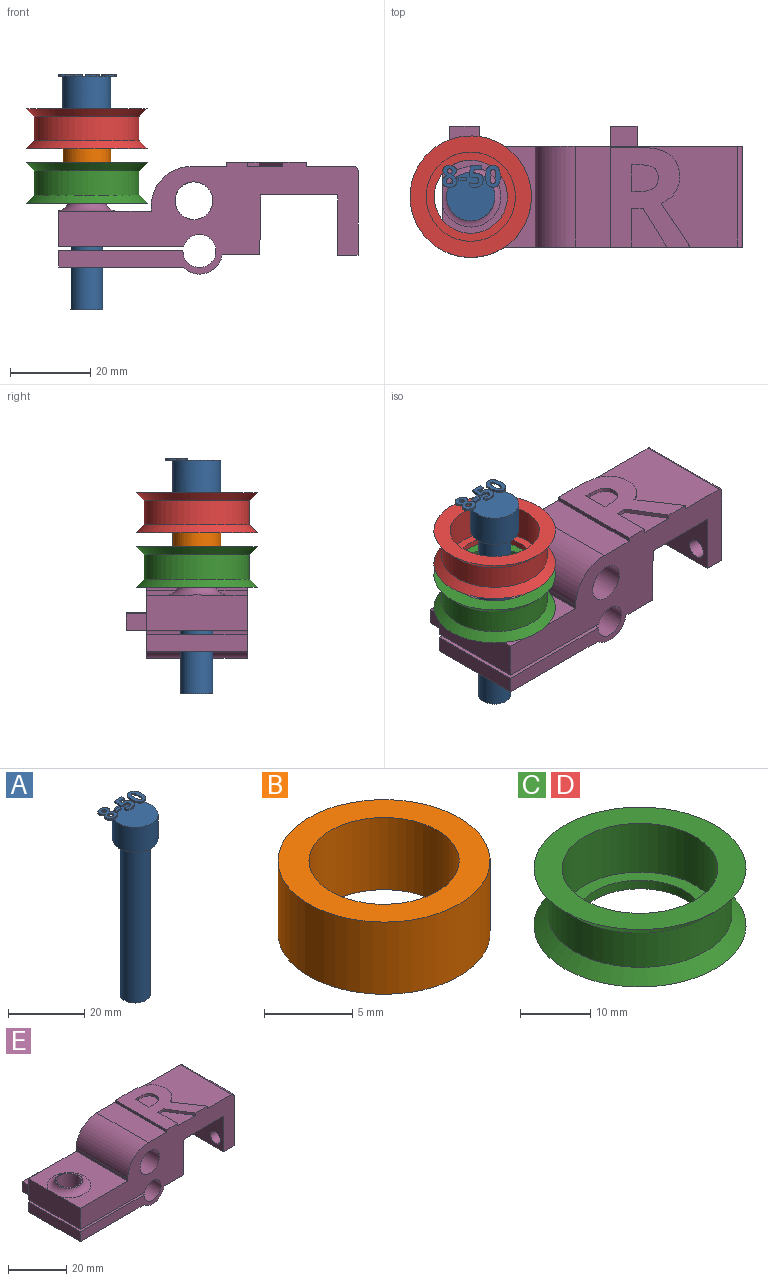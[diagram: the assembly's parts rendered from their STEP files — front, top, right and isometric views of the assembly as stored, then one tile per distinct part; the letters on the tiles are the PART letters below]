
ASSEMBLY  parts=5 mates=4
PART A: 86 faces, bbox 14.5x13.7x58.5 mm
  f0: plane 12x12mm, normal (0,0,1), area 99.4mm2, adj f5,f22,f23,f24,f25,f26,f40,f41
  f1: plane 1x0.26mm, normal (0,0,1), area 0.1mm2, adj f5,f46,f47,f48,f49
  f2: plane 0.85x0.68mm, normal (0,0,1), area 0.2mm2, adj f5,f29,f30,f31
  f3: cylinder r=4mm len=50mm, axis (0,0,-1), area 1256.6mm2, adj f4,f6
  f4: plane 8x8mm, normal (0,0,-1), area 50.3mm2, adj f3
  f5: cylinder r=6mm len=12mm, axis (0,0,-1), area 301.6mm2, adj f0,f1,f2,f6,f39,f45,f67,f85
  f6: plane 12x12mm, normal (0,0,-1), area 62.8mm2, adj f3,f5
  f7: extruded ~0.5x0.46mm, area 0.2mm2, adj f8,f37,f38,f39
  f8: extruded ~0.5x0.46mm, area 0.2mm2, adj f7,f9,f38,f39
  f9: extruded ~0.5x0.39mm, area 0.2mm2, adj f8,f10,f38,f39
  f10: extruded ~0.5x0.4mm, area 0.2mm2, adj f9,f11,f38,f39
  f11: extruded ~0.5x0.49mm, area 0.3mm2, adj f10,f12,f38,f39
  f12: extruded ~0.5x0.5mm, area 0.3mm2, adj f11,f13,f38,f39
  f13: extruded ~0.5x0.39mm, area 0.2mm2, adj f12,f37,f38,f39
  f14: extruded ~1.22x0.5mm, area 0.6mm2, adj f15,f35,f38,f39
  f15: extruded ~1.22x0.5mm, area 0.6mm2, adj f14,f16,f38,f39
  f16: extruded ~0.91x0.5mm, area 0.5mm2, adj f15,f17,f38,f39
  f17: extruded ~0.71x0.5mm, area 0.4mm2, adj f16,f18,f38,f39
  f18: extruded ~0.65x0.61mm, area 0.4mm2, adj f17,f19,f38,f39
  f19: extruded ~0.77x0.62mm, area 0.5mm2, adj f18,f20,f38,f39
  f20: extruded ~0.8x0.5mm, area 0.4mm2, adj f19,f21,f38,f39
  f21: extruded ~1.04x0.5mm, area 0.6mm2, adj f20,f22,f38,f39
  f22: extruded ~1.36x0.5mm, area 0.7mm2, adj f0,f21,f23,f38,f39
  f23: extruded ~1.33x0.5mm, area 0.7mm2, adj f0,f22,f24,f38
  f24: extruded ~1.04x0.51mm, area 0.6mm2, adj f0,f23,f25,f38
  f25: extruded ~0.75x0.5mm, area 0.4mm2, adj f0,f24,f26,f38
  f26: extruded ~0.85x0.66mm, area 0.5mm2, adj f0,f25,f27,f38,f39
  f27: extruded ~0.72x0.56mm, area 0.5mm2, adj f26,f28,f38,f39
  f28: extruded ~0.72x0.5mm, area 0.4mm2, adj f27,f35,f38,f39
  f29: extruded ~0.5x0.45mm, area 0.3mm2, adj f2,f30,f36,f38,f39
  f30: extruded ~0.5x0.47mm, area 0.3mm2, adj f2,f29,f31,f38
  f31: extruded ~0.62x0.5mm, area 0.3mm2, adj f2,f30,f32,f38,f39
  f32: extruded ~0.59x0.5mm, area 0.3mm2, adj f31,f33,f38,f39
  f33: extruded ~0.5x0.48mm, area 0.3mm2, adj f32,f34,f38,f39
  f34: extruded ~0.89x0.77mm, area 0.6mm2, adj f33,f36,f38,f39
  f35: extruded ~0.93x0.5mm, area 0.5mm2, adj f14,f28,f38,f39
  f36: extruded ~0.66x0.5mm, area 0.4mm2, adj f29,f34,f38,f39
  f37: extruded ~0.5x0.39mm, area 0.2mm2, adj f7,f13,f38,f39
  f38: plane 5.4x3.69mm, normal (0,0,1), area 12.7mm2, adj f7,f8,f9,f10,f11,f12,f13,f14
  f39: plane 5.4x3.53mm, normal (0,0,-1), area 10.2mm2, adj f5,f7,f8,f9,f10,f11,f12,f13
  f40: plane 0.9x0.5mm, normal (-1,0,0), area 0.4mm2, adj f0,f41,f43,f44
  f41: plane 1.93x0.5mm, normal (0,-1,0), area 1mm2, adj f0,f40,f42,f44
  f42: plane 0.9x0.5mm, normal (1,0,0), area 0.4mm2, adj f0,f41,f43,f44
  f43: plane 1.93x0.5mm, normal (0,1,0), area 1mm2, adj f0,f40,f42,f44
  f44: plane 1.93x0.9mm, normal (0,0,1), area 1.7mm2, adj f40,f41,f42,f43
  f45: plane 0.76x0.31mm, normal (0,0,-1), area 0mm2, adj f5,f46
  f46: extruded ~1.21x0.5mm, area 0.7mm2, adj f0,f1,f45,f47,f65,f66
  f47: extruded ~0.54x0.5mm, area 0.3mm2, adj f1,f46,f48,f66
  f48: plane 0.5x0.13mm, normal (-0.2,0.98,0), area 0.1mm2, adj f1,f47,f49,f66
  f49: plane 1.03x0.5mm, normal (1,-0.09,0), area 0.5mm2, adj f1,f48,f50,f66,f67
  f50: plane 1.88x0.5mm, normal (0,-1,0), area 0.9mm2, adj f49,f51,f66,f67
  f51: plane 0.94x0.5mm, normal (1,0,0), area 0.5mm2, adj f50,f52,f66,f67
  f52: plane 2.85x0.5mm, normal (0,1,0), area 1.4mm2, adj f51,f53,f66,f67
  f53: plane 2.68x0.5mm, normal (-1,0.07,0), area 1.3mm2, adj f0,f52,f54,f66,f67
  f54: plane 0.5x0.44mm, normal (-0.47,-0.88,0), area 0.3mm2, adj f0,f53,f55,f66
  f55: extruded ~0.5x0.37mm, area 0.2mm2, adj f0,f54,f56,f66
  f56: extruded ~0.5x0.42mm, area 0.2mm2, adj f0,f55,f57,f66
  f57: extruded ~1.05x0.8mm, area 0.8mm2, adj f0,f56,f58,f66
  f58: extruded ~1.02x0.83mm, area 0.8mm2, adj f0,f57,f59,f66
  f59: extruded ~0.72x0.5mm, area 0.4mm2, adj f0,f58,f60,f66
  f60: extruded ~0.66x0.5mm, area 0.4mm2, adj f0,f59,f61,f66
  f61: plane 0.96x0.5mm, normal (-1,0,0), area 0.5mm2, adj f0,f60,f62,f66
  f62: extruded ~1.42x0.5mm, area 0.7mm2, adj f0,f61,f63,f66
  f63: extruded ~1.55x0.5mm, area 0.8mm2, adj f0,f62,f64,f66
  f64: extruded ~1.36x0.54mm, area 0.8mm2, adj f0,f63,f65,f66
  f65: extruded ~1.17x0.5mm, area 0.6mm2, adj f0,f46,f64,f66
  f66: plane 5.33x3.51mm, normal (0,0,1), area 10.9mm2, adj f46,f47,f48,f49,f50,f51,f52,f53
  f67: plane 2.97x1.71mm, normal (0,0,-1), area 3.5mm2, adj f5,f49,f50,f51,f52,f53
  f68: extruded ~1.39x0.5mm, area 0.7mm2, adj f69,f83,f84,f85
  f69: extruded ~1.39x0.5mm, area 0.7mm2, adj f68,f70,f84,f85
  f70: extruded ~0.56x0.5mm, area 0.4mm2, adj f69,f71,f84,f85
  f71: extruded ~0.56x0.5mm, area 0.4mm2, adj f70,f72,f84,f85
  f72: extruded ~1.39x0.5mm, area 0.7mm2, adj f71,f73,f84,f85
  f73: extruded ~1.38x0.5mm, area 0.7mm2, adj f72,f74,f84,f85
  f74: extruded ~0.56x0.5mm, area 0.4mm2, adj f73,f83,f84,f85
  f75: extruded ~2.04x0.5mm, area 1.1mm2, adj f76,f82,f84,f85
  f76: extruded ~2.02x0.5mm, area 1.1mm2, adj f75,f77,f84,f85
  f77: extruded ~1.38x0.69mm, area 0.8mm2, adj f76,f78,f84,f85
  f78: extruded ~1.38x0.66mm, area 0.8mm2, adj f77,f79,f84,f85
  f79: extruded ~2.05x0.5mm, area 1.1mm2, adj f78,f80,f84,f85
  f80: extruded ~2.02x0.5mm, area 1mm2, adj f0,f79,f81,f84,f85
  f81: extruded ~1.37x0.68mm, area 0.8mm2, adj f0,f80,f82,f84
  f82: extruded ~1.39x0.66mm, area 0.8mm2, adj f0,f75,f81,f84,f85
  f83: extruded ~0.56x0.5mm, area 0.4mm2, adj f68,f74,f84,f85
  f84: plane 5.41x3.68mm, normal (0,0,1), area 12.1mm2, adj f68,f69,f70,f71,f72,f73,f74,f75
  f85: plane 5.41x3.68mm, normal (0,0,-1), area 10.3mm2, adj f5,f68,f69,f70,f71,f72,f73,f74
PART B: 4 faces, bbox 12x12x5 mm
  f0: cylinder r=4.25mm len=8.5mm, axis (0,0,-1), area 133.5mm2, adj f2,f3
  f1: cylinder r=6mm len=12mm, axis (0,0,-1), area 188.5mm2, adj f2,f3
  f2: plane 12x12mm, normal (0,0,1), area 56.4mm2, adj f0,f1
  f3: plane 12x12mm, normal (0,0,-1), area 56.4mm2, adj f0,f1
PART C: 8 faces, bbox 30.2x30.2x10 mm
  f0: plane 30.2x30.2mm, normal (0,0,1), area 329.2mm2, adj f1,f7
  f1: cylinder r=11.1mm len=22.2mm, axis (0,0,-1), area 592.8mm2, adj f0,f2
  f2: plane 22.2x22.2mm, normal (0,0,1), area 126.9mm2, adj f1,f3
  f3: cylinder r=9.1mm len=18.2mm, axis (0,0,-1), area 85.8mm2, adj f2,f4
  f4: plane 30.2x30.2mm, normal (0,0,-1), area 456.2mm2, adj f3,f5
  f5: cone r=13.1mm half-angle=45deg, axis (0,0,-1), area 250.6mm2, adj f4,f6
  f6: cylinder r=13.1mm len=26.2mm, axis (0,0,-1), area 493.9mm2, adj f5,f7
  f7: cone r=15.1mm half-angle=45deg, axis (0,0,1), area 250.6mm2, adj f0,f6
PART D: same geometry as C
PART E: 56 faces, bbox 77.9x30x27.7 mm
  f0: plane 40.42x25mm, normal (0,0,1), area 617.1mm2, adj f14,f15,f25,f27,f40,f41,f42,f43
  f1: plane 9.51x8.71mm, normal (0,0,1), area 54.7mm2, adj f14,f37,f38,f39
  f2: plane 25x4.12mm, normal (-1,0,0), area 103mm2, adj f5,f14,f15,f19
  f3: cylinder r=4.17mm len=8.35mm, axis (0,0,1), area 108.1mm2, adj f5,f19
  f4: plane 25x9.34mm, normal (0,0,-1), area 233.4mm2, adj f13,f14,f15,f17
  f5: plane 30.88x25mm, normal (0,0,-1), area 717.2mm2, adj f2,f3,f14,f15,f17
  f6: plane 25x8.82mm, normal (-1,0,0), area 219.6mm2, adj f7,f14,f15,f20,f24
  f7: plane 25x23mm, normal (0,0,1), area 400mm2, adj f6,f8,f14,f15,f24
  f8: plane 25x1.1mm, normal (-1,0,0), area 27.5mm2, adj f7,f14,f15,f25
  f9: plane 25x21.09mm, normal (1,0,0), area 493.5mm2, adj f10,f14,f15,f22,f23,f27
  f10: plane 25x5mm, normal (0,0,-1), area 125mm2, adj f9,f11,f14,f15
  f11: plane 25x15mm, normal (-1,0,0), area 341.3mm2, adj f10,f12,f14,f15,f22,f23
  f12: plane 25x19.2mm, normal (0,0,-1), area 480mm2, adj f11,f13,f14,f15
  f13: plane 25x14.91mm, normal (1,0,-0.01), area 372.8mm2, adj f4,f12,f14,f15
  f14: plane 74.42x27.75mm, normal (0,-1,0), area 1061.7mm2, adj f0,f1,f2,f4,f5,f6,f7,f8
  f15: plane 74.42x26.75mm, normal (0,1,0), area 990.6mm2, adj f0,f2,f4,f5,f6,f7,f8,f9
  f16: cylinder r=4.17mm len=10.78mm, axis (0,0,1), area 282.8mm2, adj f20,f21
  f17: cylinder r=5.75mm len=25mm, axis (0,-1,0), area 315.9mm2, adj f4,f5,f14,f15
  f18: cylinder r=4.1mm len=25mm, axis (0,-1,0), area 618.7mm2, adj f14,f15,f19,f20
  f19: plane 30.91x25mm, normal (0,0,1), area 718.1mm2, adj f2,f3,f14,f15,f18
  f20: plane 31.07x30mm, normal (0,0,-1), area 758.4mm2, adj f6,f14,f15,f16,f18,f29,f30,f31
  f21: plane 9.35x9.35mm, normal (0,0,1), area 13.9mm2, adj f16,f24
  f22: cylinder r=2.43mm len=5mm, axis (1,0,0), area 76.2mm2, adj f9,f11
  f23: cylinder r=2.2mm len=5mm, axis (1,0,0), area 69.1mm2, adj f9,f11
  f24: torus R=7.5mm, axis (0,0,-1), area 134.6mm2, adj f6,f7,f21
  f25: cylinder r=10mm len=25mm, axis (0,-1,0), area 392.7mm2, adj f0,f8,f14,f15
  f26: cylinder r=4.68mm len=25mm, axis (0,-1,0), area 735.2mm2, adj f14,f15
  f27: cylinder r=1mm len=25mm, axis (0,-1,0), area 39.3mm2, adj f0,f9,f14,f15
  f28: plane 7.3x5mm, normal (0,0,1), area 36.5mm2, adj f15,f29,f30,f31
  f29: plane 5x4.12mm, normal (-1,0,0), area 20.6mm2, adj f15,f20,f28,f31
  f30: plane 5x4.12mm, normal (1,0,0), area 20.6mm2, adj f15,f20,f28,f31
  f31: plane 7.3x4.12mm, normal (0,1,0), area 30.1mm2, adj f20,f28,f29,f30
  f32: plane 6.63x5mm, normal (0,0,1), area 33.2mm2, adj f15,f33,f35,f36
  f33: plane 5x4.5mm, normal (-1,0,0), area 22.5mm2, adj f15,f32,f34,f36
  f34: plane 6.63x5mm, normal (0,0,-1), area 33.2mm2, adj f15,f33,f35,f36
  f35: plane 5x4.5mm, normal (1,0,0), area 22.5mm2, adj f15,f32,f34,f36
  f36: plane 6.63x4.5mm, normal (0,1,0), area 29.9mm2, adj f32,f33,f34,f35
  f37: plane 9.51x1mm, normal (1,0,0), area 9.5mm2, adj f1,f14,f38,f54
  f38: plane 2.79x1mm, normal (0,-1,0), area 2.8mm2, adj f1,f37,f39,f54
  f39: plane 9.51x5.92mm, normal (-0.85,-0.53,0), area 11.2mm2, adj f1,f14,f38,f54
  f40: extruded ~10.8x7.29mm, area 13mm2, adj f0,f14,f41,f54
  f41: extruded ~3.41x2.67mm, area 4.4mm2, adj f0,f40,f42,f54
  f42: extruded ~3.89x1.2mm, area 4.1mm2, adj f0,f41,f43,f54
  f43: extruded ~5.59x2.42mm, area 6.3mm2, adj f0,f42,f44,f54
  f44: extruded ~7.48x1.84mm, area 7.8mm2, adj f0,f43,f45,f54
  f45: plane 7.22x1mm, normal (0,1,0), area 7.2mm2, adj f0,f44,f46,f54
  f46: plane 24.79x1mm, normal (-1,0,0), area 24.8mm2, adj f0,f14,f45,f54
  f47: plane 1.69x1mm, normal (0,1,0), area 1.7mm2, adj f48,f53,f54,f55
  f48: plane 6.7x1mm, normal (1,0,0), area 6.7mm2, adj f47,f49,f54,f55
  f49: plane 1.6x1mm, normal (0,-1,0), area 1.6mm2, adj f48,f50,f54,f55
  f50: extruded ~3.75x1mm, area 3.9mm2, adj f49,f51,f54,f55
  f51: extruded ~2.51x1.21mm, area 2.9mm2, adj f50,f52,f54,f55
  f52: extruded ~2.61x1.19mm, area 3mm2, adj f51,f53,f54,f55
  f53: extruded ~3.68x1mm, area 3.8mm2, adj f47,f52,f54,f55
  f54: plane 24.79x19.8mm, normal (0,0,1), area 300mm2, adj f14,f37,f38,f39,f40,f41,f42,f43
  f55: plane 6.7x6.56mm, normal (0,0,1), area 38.8mm2, adj f47,f48,f49,f50,f51,f52,f53
PLACE A t=(-103.78,-12.5,-13.6)mm
PLACE B rot(axis=(1,0,0),180deg) t=(-103.78,-12.5,26.4)mm
PLACE C t=(-103.78,-12.5,18.1)mm
PLACE D t=(-103.78,-12.5,31.6)mm
PLACE E at identity
MATE fastened A.f3 <-> D.f1  axis (0,0,-1) through (-103.78,-12.5,36.4)mm
MATE fastened B.f0 <-> C.f1  axis (0,0,1) through (-103.78,-12.5,21.4)mm
MATE fastened C.f1 <-> E.f3  axis (0,0,-1) through (-103.78,-12.5,12.9)mm
MATE fastened D.f1 <-> B.f0  axis (0,0,-1) through (-103.78,-12.5,26.4)mm
